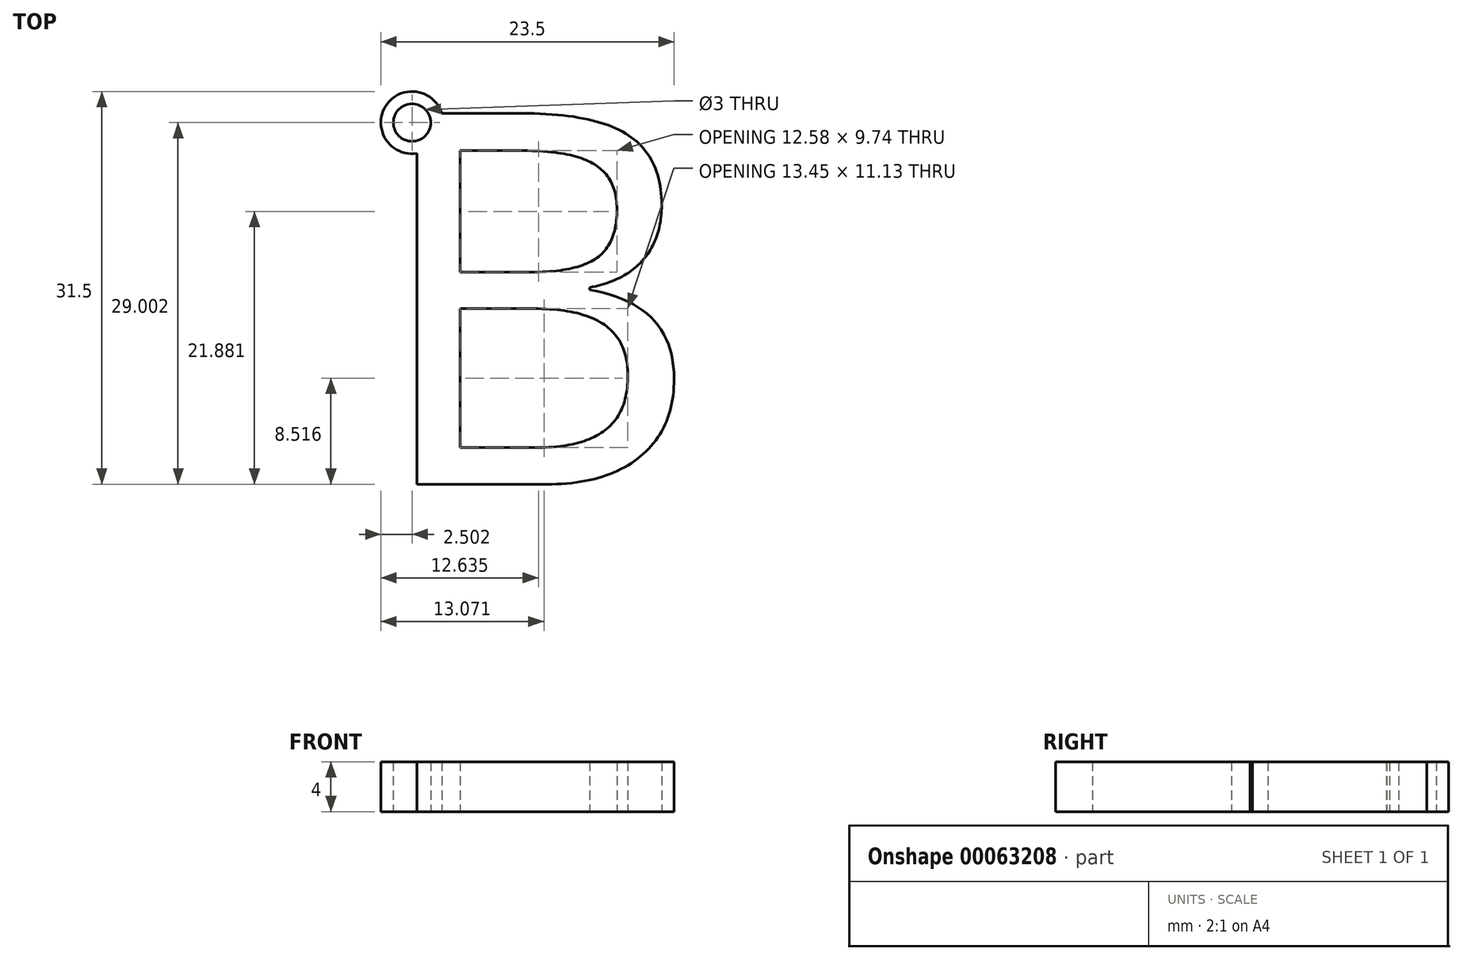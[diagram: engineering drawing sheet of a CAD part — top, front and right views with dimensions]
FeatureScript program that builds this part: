
annotation { "Feature Type Name" : "Feature", "Feature Type Description" : "" }
export const myFeature = defineFeature(function(context is Context, id is Id, definition is map)
    precondition{}
    {
        {
            var Q0;
            Q0=qCreatedBy(makeId("Top.planeOp"),FACE);
            var sketch = newSketch(context, id + "F0", { "sketchPlane" : qUnion([Q0])});
            skText(sketch, "E0", { "text": "B", "fontName": "OpenSans-Regular.ttf"});
            skCircle(sketch, "E1", {"center": v(-30.89, 20.58) * mm, "radius": 1.5 * mm});
            skCircle(sketch, "E2", {"center": v(-30.89, 20.58) * mm, "radius": 2.5 * mm});
            const initialGuessF0  = {"E0": [-0.03459, -0.00842, 1, 0, 0.03]};
            skSetInitialGuess(sketch, initialGuessF0);
            skSolve(sketch);
        }
        {
            var Q0;
            Q0 = qSketchRegion(id + "F0", true);
            extrude(context, id + "F1", {"entities" : qUnion([Q0]), "depth" : 4 * mm});
        }
    });
